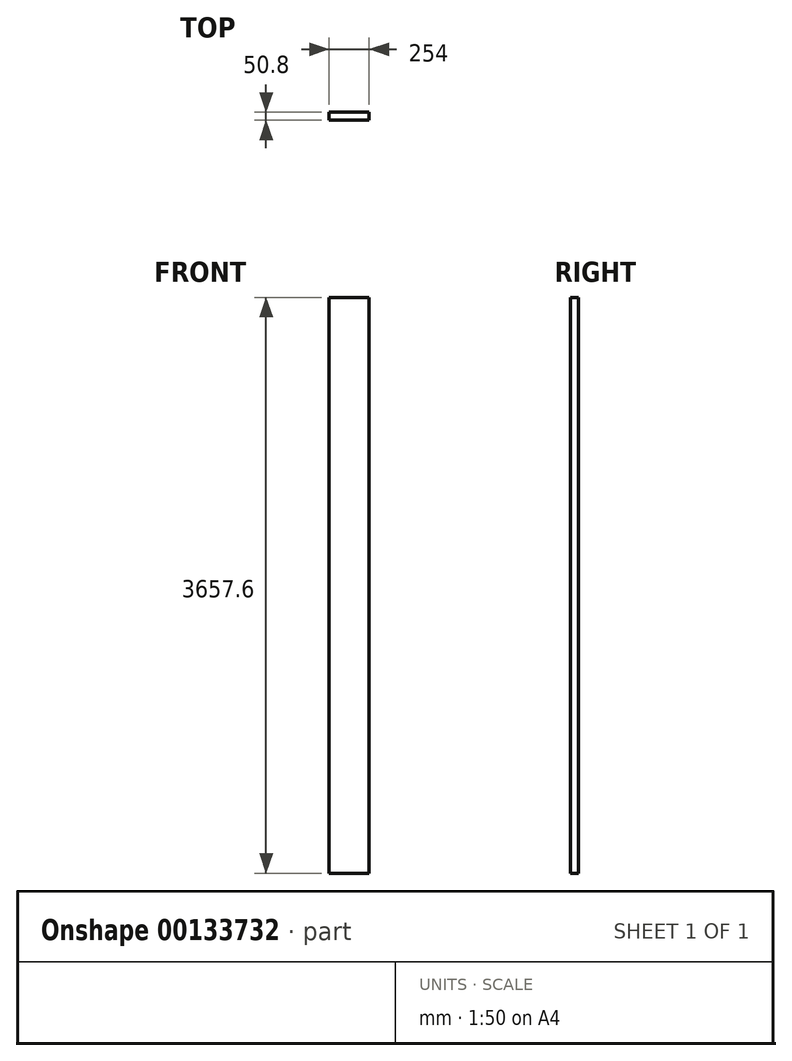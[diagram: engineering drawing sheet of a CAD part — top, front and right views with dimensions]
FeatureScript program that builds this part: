
annotation { "Feature Type Name" : "Feature", "Feature Type Description" : "" }
export const myFeature = defineFeature(function(context is Context, id is Id, definition is map)
    precondition{}
    {
        {
            var Q0;
            Q0=qCreatedBy(makeId("Top.planeOp"),FACE);
            var sketch = newSketch(context, id + "F0", { "sketchPlane" : qUnion([Q0])});
            skLineSegment(sketch, "E0.bottom", {"start": v(0, 0) * mm, "end": v(254, 0) * mm});
            skLineSegment(sketch, "E0.top", {"start": v(0, -50.8) * mm, "end": v(254, -50.8) * mm});
            skLineSegment(sketch, "E0.left", {"start": v(0, 0) * mm, "end": v(0, -50.8) * mm});
            skLineSegment(sketch, "E0.right", {"start": v(254, 0) * mm, "end": v(254, -50.8) * mm});
            skSolve(sketch);
        }
        {
            var Q0;
            Q0 = qSketchRegion(id + "F0", true);
            extrude(context, id + "F1", {"entities" : qUnion([Q0]), "depth" : 3657.6 * mm});
        }
    });
